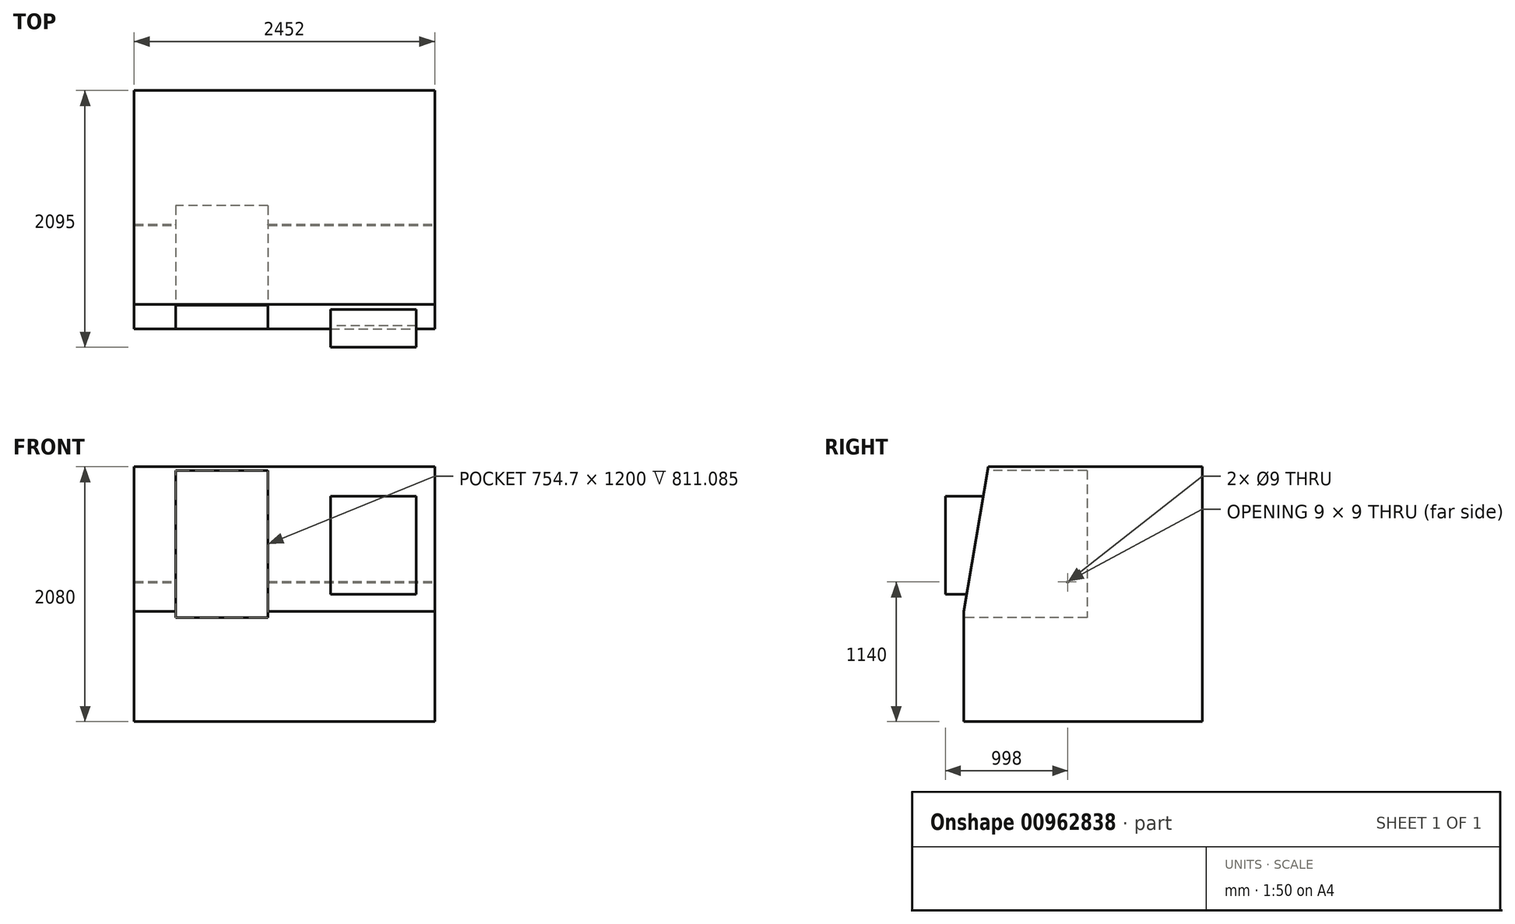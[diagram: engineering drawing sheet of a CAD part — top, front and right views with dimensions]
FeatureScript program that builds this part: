
annotation { "Feature Type Name" : "Feature", "Feature Type Description" : "" }
export const myFeature = defineFeature(function(context is Context, id is Id, definition is map)
    precondition{}
    {
        {
            var Q0;
            Q0=qCreatedBy(makeId("Front.planeOp"),FACE);
            var sketch = newSketch(context, id + "F0", { "sketchPlane" : qUnion([Q0])});
            skLineSegment(sketch, "E0.bottom", {"start": v(1226, 1040) * mm, "end": v(-1226, 1040) * mm});
            skLineSegment(sketch, "E0.top", {"start": v(1226, -1040) * mm, "end": v(-1226, -1040) * mm});
            skLineSegment(sketch, "E0.left", {"start": v(1226, 1040) * mm, "end": v(1226, -1040) * mm});
            skLineSegment(sketch, "E0.right", {"start": v(-1226, 1040) * mm, "end": v(-1226, -1040) * mm});
            skPoint(sketch, "E0.middle", {"position": v(0, 0) * mm});
            skSolve(sketch);
        }
        {
            var Q0;
            Q0=makeQuery(id+"F0.imprint","IMPRINT",FACE,{"disambiguationData":[TD([[makeQuery(id+"F0.imprint","IMPRINT",EDGE,{"derivedFrom":sQuery(id+"F0.wireOp",EDGE,"E0.bottom")}),1.0]])]});
            extrude(context, id + "F1", {"entities" : qUnion([Q0]), "endBound" : BoundingType.SYMMETRIC, "depth" : (130 + 1257 + 208 + 350) * mm, "offsetDistance" : 25 * mm});
        }
        {
            var Q0;
            Q0=makeQuery(id+"F1.opExtrude","CAP_FACE",FACE,{"disambiguationData":[OSD([sQuery(id+"F0.wireOp",EDGE,"E0.bottom"),sQuery(id+"F0.wireOp",EDGE,"E0.top"),sQuery(id+"F0.wireOp",EDGE,"E0.left"),sQuery(id+"F0.wireOp",EDGE,"E0.right")])],"isStart":false});
            var sketch = newSketch(context, id + "F2", { "sketchPlane" : qUnion([Q0])});
            skLineSegment(sketch, "E1.bottom", {"start": v(1076, 0) * mm, "end": v(376, 0) * mm});
            skLineSegment(sketch, "E1.top", {"start": v(1076, 800) * mm, "end": v(376, 800) * mm});
            skLineSegment(sketch, "E1.left", {"start": v(1076, 0) * mm, "end": v(1076, 800) * mm});
            skLineSegment(sketch, "E1.right", {"start": v(376, 0) * mm, "end": v(376, 800) * mm});
            skPoint(sketch, "E1.middle", {"position": v(726, 400) * mm});
            skSolve(sketch);
        }
        {
            var Q0;
            Q0=makeQuery(id+"F1.opExtrude","SWEPT_FACE",FACE,{"disambiguationData":[OSD([sQuery(id+"F0.wireOp",EDGE,"E0.left")])]});
            var sketch = newSketch(context, id + "F3", { "sketchPlane" : qUnion([Q0])});
            skLineSegment(sketch, "E2", {"start": v(-972.5, -140) * mm, "end": v(-772.5, 1040) * mm});
            skSolve(sketch);
        }
        {
            var Q0;
            {var subQ0=sQuery(id+"F3.wireOp",EDGE,"E2");Q0=makeQuery(id+"F3.imprint","IMPRINT",FACE,{"disambiguationData":[TD([[makeQuery(id+"F3.imprint","IMPRINT",EDGE,{"derivedFrom":subQ0}),1.0]])]});}
            extrude(context, id + "F4", {"entities" : qUnion([Q0]), "operationType" : NewBodyOperationType.REMOVE, "oppositeDirection" : true, "depth" : 2940 * mm, "offsetDistance" : 25 * mm});
        }
        {
            var Q0;
            Q0 = qSketchRegion(id + "F2", true);
            extrude(context, id + "F5", {"entities" : qUnion([Q0]), "depth" : 150 * mm, "offsetDistance" : 25 * mm});
        }
        {
            var Q0;
            Q0=makeQuery(id+"F5.opExtrude","CAP_FACE",FACE,{"disambiguationData":[OSD([sQuery(id+"F2.wireOp",EDGE,"E1.bottom"),sQuery(id+"F2.wireOp",EDGE,"E1.top"),sQuery(id+"F2.wireOp",EDGE,"E1.left"),sQuery(id+"F2.wireOp",EDGE,"E1.right")])],"isStart":true});
            var sketch = newSketch(context, id + "F6", { "sketchPlane" : qUnion([Q0])});
            skLineSegment(sketch, "E3.0.0", {"start": v(-1076, 800) * mm, "end": v(-1076, 0) * mm});
            skLineSegment(sketch, "E3.0.1", {"start": v(-1076, 0) * mm, "end": v(-376, 0) * mm});
            skLineSegment(sketch, "E3.0.2", {"start": v(-376, 0) * mm, "end": v(-376, 800) * mm});
            skLineSegment(sketch, "E3.0.3", {"start": v(-376, 800) * mm, "end": v(-1076, 800) * mm});
            skSolve(sketch);
        }
        {
            var Q0;
            Q0=makeQuery(id+"F6.imprint","IMPRINT",FACE,{"disambiguationData":[TD([[makeQuery(id+"F6.imprint","IMPRINT",EDGE,{"derivedFrom":sQuery(id+"F6.wireOp",EDGE,"E3.0.0")}),-1.0]])]});
            extrude(context, id + "F7", {"entities" : qUnion([Q0]), "operationType" : NewBodyOperationType.ADD, "endBound" : BoundingType.UP_TO_NEXT, "depth" : 25 * mm, "offsetDistance" : 25 * mm});
        }
        {
            var Q0;
            Q0=makeQuery(id+"F1.opExtrude","CAP_FACE",FACE,{"disambiguationData":[OSD([sQuery(id+"F0.wireOp",EDGE,"E0.bottom"),sQuery(id+"F0.wireOp",EDGE,"E0.top"),sQuery(id+"F0.wireOp",EDGE,"E0.left"),sQuery(id+"F0.wireOp",EDGE,"E0.right")])],"isStart":false});
            var sketch = newSketch(context, id + "F8", { "sketchPlane" : qUnion([Q0])});
            skLineSegment(sketch, "E4.bottom", {"start": v(-133.81, 1010) * mm, "end": v(-888.51, 1010) * mm});
            skLineSegment(sketch, "E4.top", {"start": v(-133.81, -190) * mm, "end": v(-888.51, -190) * mm});
            skLineSegment(sketch, "E4.left", {"start": v(-133.81, 1010) * mm, "end": v(-133.81, -190) * mm});
            skLineSegment(sketch, "E4.right", {"start": v(-888.51, 1010) * mm, "end": v(-888.51, -190) * mm});
            skPoint(sketch, "E4.middle", {"position": v(-511.16, 410) * mm});
            skSolve(sketch);
        }
        {
            var Q0;
            {var subQ0=sQuery(id+"F8.wireOp",EDGE,"E4.bottom");Q0=makeQuery(id+"F8.imprint","IMPRINT",FACE,{"disambiguationData":[TD([[makeQuery(id+"F8.imprint","IMPRINT",EDGE,{"derivedFrom":subQ0}),1.0]])]});}
            var Q1;
            {var subQ0=sQuery(id+"F8.wireOp",EDGE,"E4.top");Q1=makeQuery(id+"F8.imprint","IMPRINT",FACE,{"disambiguationData":[TD([[makeQuery(id+"F8.imprint","IMPRINT",EDGE,{"derivedFrom":subQ0}),-1.0]])]});}
            extrude(context, id + "F9", {"entities" : qUnion([Q0, Q1]), "operationType" : NewBodyOperationType.REMOVE, "oppositeDirection" : true, "depth" : 1006 * mm, "offsetDistance" : 25 * mm});
        }
        {
            var Q0;
            Q0=makeQuery(id+"F1.opExtrude","SWEPT_FACE",FACE,{"disambiguationData":[OSD([sQuery(id+"F0.wireOp",EDGE,"E0.left")])]});
            var sketch = newSketch(context, id + "F10", { "sketchPlane" : qUnion([Q0])});
            skPoint(sketch, "E5", {"position": v(-124.5, 100) * mm});
            skSolve(sketch);
        }
        {
            var Q0;
            Q0=sQuery(id+"F10.wireOp",VERTEX,"E5");
            var Q1;
            Q1=makeQuery(id+"F1.opExtrude","SWEPT_BODY",BODY,{"disambiguationData":[OSD([sQuery(id+"F0.wireOp",EDGE,"E0.bottom"),sQuery(id+"F0.wireOp",EDGE,"E0.top"),sQuery(id+"F0.wireOp",EDGE,"E0.left"),sQuery(id+"F0.wireOp",EDGE,"E0.right")])]});
            hole(context, id + "F11", {"style" : HoleStyle.SIMPLE, "endStyle" : HoleEndStyle.THROUGH, "holeDiameter" : 9 * mm, "majorDiameter" : 5 * mm, "isTappedThrough" : true, "tappedDepth" : 12 * mm, "tapClearance" : 3, "locations" : qUnion([Q0]), "scope" : qUnion([Q1])});
        }
    });
